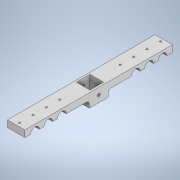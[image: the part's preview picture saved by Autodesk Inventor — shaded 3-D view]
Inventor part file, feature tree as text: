
AUTODESK INVENTOR PART (.ipt)
format: ipt  version: 2020 (Build 240168000, 168)  size: 182,784 bytes
history: native  units: mm
features: sketch x6, extrude x4, hole x2, pattern_linear x2, mirror x1, fillet x1, projected_geometry x1
ambient origin geometry x8: Origin, YZ Plane, XZ Plane, XY Plane, X Axis, Y Axis, Z Axis, Center Point
bodies: Solid1 (feature_tree)
feature tree (17):
  extrude  "Extrusion1"  Depth=26.0mm
  extrude  "Extrusion2"  Depth=28.0mm
  extrude  "Extrusion3"  Depth=20.25mm
  hole  "Hole1"  [1 undecoded]
  extrude  "Extrusion4"  Depth=75.0mm
  hole  "Hole2"  [1 undecoded]
  pattern_linear  "Rectangular Pattern1"  Count1=2  [1 undecoded]
  pattern_linear  "Rectangular Pattern2"  Count1=2  [1 undecoded]
  mirror  "Mirror1"
  fillet  "Fillet1"  Radius=20.0mm
  sketch  "Sketch1"  dims[d0=220.0mm d1=26.0mm]
  sketch  "Sketch3"  dims[d2=10.0mm d3=0.0mm d4=28.0mm]
  sketch  "Sketch4"  dims[d5=10.0mm d6=0.0mm d7=20.25mm]
  sketch  "Sketch5"  dims[d8=20.25mm d9=0.0mm d10=0.0mm]
  sketch  "Sketch6"  dims[d11=4.3mm d12=6.0mm d13=9.4mm d14=2.0mm d15=90.0deg d16=8.0mm d17=90.0deg d18=75.0mm]
  sketch  "Sketch7"  dims[d19=13.2mm d20=0.0mm d21=0.0mm d22=20.0mm d23=2.459mm d24=6.0mm d25=9.4mm d26=2.0mm d27=90.0deg d28=8.8mm d29=90.0deg d30=20.0mm d32=20.0mm d33=20.0mm d35=20.0mm d36=20.0mm d38=20.0mm d39=20.0mm d41=20.0mm d42=5.0mm]
  projected_geometry  "Projected Loop1"
note: 4 required parameter values undecoded (feature->parameter linkage not recoverable at this tier; creation-order binding heuristic only, values carry confidence <= 0.55)
